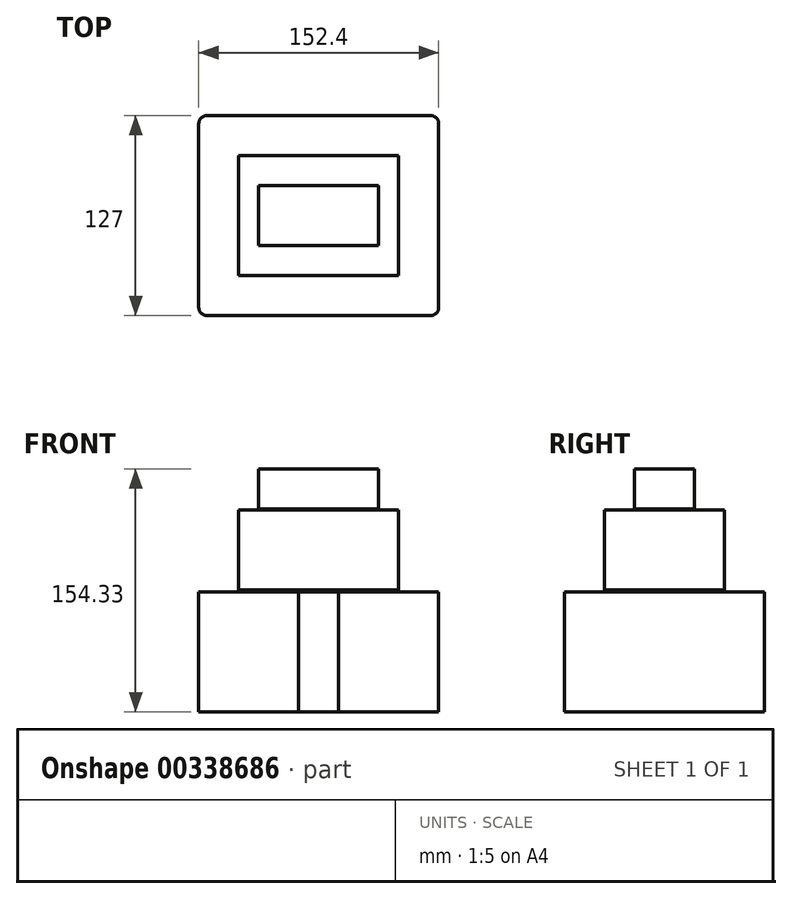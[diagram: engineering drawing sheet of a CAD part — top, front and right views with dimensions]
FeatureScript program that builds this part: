
annotation { "Feature Type Name" : "Feature", "Feature Type Description" : "" }
export const myFeature = defineFeature(function(context is Context, id is Id, definition is map)
    precondition{}
    {
        {
            var Q0;
            Q0=qCreatedBy(makeId("Front.planeOp"),FACE);
            var sketch = newSketch(context, id + "F0", { "sketchPlane" : qUnion([Q0])});
            skLineSegment(sketch, "E0.bottom", {"start": v(-76.2, 38.1) * mm, "end": v(76.2, 38.1) * mm});
            skLineSegment(sketch, "E0.top", {"start": v(-76.2, -38.1) * mm, "end": v(76.2, -38.1) * mm});
            skLineSegment(sketch, "E0.left", {"start": v(-76.2, 38.1) * mm, "end": v(-76.2, -38.1) * mm});
            skLineSegment(sketch, "E0.right", {"start": v(76.2, 38.1) * mm, "end": v(76.2, -38.1) * mm});
            skPoint(sketch, "E0.middle", {"position": v(0, 0) * mm});
            skSolve(sketch);
        }
        {
            var Q0;
            Q0=makeQuery(id+"F0.imprint","IMPRINT",FACE,{"disambiguationData":[TD([[makeQuery(id+"F0.imprint","IMPRINT",EDGE,{"derivedFrom":sQuery(id+"F0.wireOp",EDGE,"E0.bottom")}),-1.0]])]});
            extrude(context, id + "F1", {"entities" : qUnion([Q0]), "endBound" : BoundingType.SYMMETRIC, "depth" : 127 * mm});
        }
        {
            var Q0;
            Q0=qCreatedBy(makeId("Front.planeOp"),FACE);
            var sketch = newSketch(context, id + "F2", { "sketchPlane" : qUnion([Q0])});
            skLineSegment(sketch, "E1.bottom", {"start": v(-50.8, 39.3) * mm, "end": v(50.8, 39.3) * mm});
            skLineSegment(sketch, "E1.top", {"start": v(-50.8, 90.1) * mm, "end": v(50.8, 90.1) * mm});
            skLineSegment(sketch, "E1.left", {"start": v(-50.8, 39.3) * mm, "end": v(-50.8, 90.1) * mm});
            skLineSegment(sketch, "E1.right", {"start": v(50.8, 39.3) * mm, "end": v(50.8, 90.1) * mm});
            skPoint(sketch, "E1.middle", {"position": v(0, 64.7) * mm});
            skSolve(sketch);
        }
        {
            var Q0;
            Q0=makeQuery(id+"F2.imprint","IMPRINT",FACE,{"disambiguationData":[TD([[makeQuery(id+"F2.imprint","IMPRINT",EDGE,{"derivedFrom":sQuery(id+"F2.wireOp",EDGE,"E1.bottom")}),1.0]])]});
            extrude(context, id + "F3", {"entities" : qUnion([Q0]), "endBound" : BoundingType.SYMMETRIC, "depth" : 76.2 * mm});
        }
        {
            var Q0;
            Q0=qCreatedBy(makeId("Front.planeOp"),FACE);
            var sketch = newSketch(context, id + "F4", { "sketchPlane" : qUnion([Q0])});
            skLineSegment(sketch, "E2.bottom", {"start": v(-38.1, 116.23) * mm, "end": v(38.1, 116.23) * mm});
            skLineSegment(sketch, "E2.top", {"start": v(-38.1, 90.83) * mm, "end": v(38.1, 90.83) * mm});
            skLineSegment(sketch, "E2.left", {"start": v(-38.1, 116.23) * mm, "end": v(-38.1, 90.83) * mm});
            skLineSegment(sketch, "E2.right", {"start": v(38.1, 116.23) * mm, "end": v(38.1, 90.83) * mm});
            skPoint(sketch, "E2.middle", {"position": v(0, 103.53) * mm});
            skSolve(sketch);
        }
        {
            var Q0;
            Q0 = qSketchRegion(id + "F4", true);
            extrude(context, id + "F5", {"entities" : qUnion([Q0]), "endBound" : BoundingType.SYMMETRIC, "depth" : 38.1 * mm});
        }
        {
            var Q0;
            Q0=makeQuery(id+"F1.opExtrude","CAP_EDGE",EDGE,{"disambiguationData":[OSD([sQuery(id+"F0.wireOp",EDGE,"E0.left")])],"isStart":false});
            var Q1;
            Q1=makeQuery(id+"F1.opExtrude","CAP_EDGE",EDGE,{"disambiguationData":[OSD([sQuery(id+"F0.wireOp",EDGE,"E0.right")])],"isStart":false});
            var Q2;
            Q2=makeQuery(id+"F1.opExtrude","CAP_EDGE",EDGE,{"disambiguationData":[OSD([sQuery(id+"F0.wireOp",EDGE,"E0.right")])],"isStart":true});
            var Q3;
            Q3=makeQuery(id+"F1.opExtrude","CAP_EDGE",EDGE,{"disambiguationData":[OSD([sQuery(id+"F0.wireOp",EDGE,"E0.left")])],"isStart":true});
            fillet(context, id + "F6", {"entities" : qUnion([Q0, Q1, Q2, Q3]), "radius" : 5.08 * mm, "tangentPropagation" : true, "allowEdgeOverflow" : false});
        }
        {
            var Q0;
            Q0=makeQuery(id+"F1.opExtrude","CAP_FACE",FACE,{"disambiguationData":[OSD([sQuery(id+"F0.wireOp",EDGE,"E0.bottom"),sQuery(id+"F0.wireOp",EDGE,"E0.top"),sQuery(id+"F0.wireOp",EDGE,"E0.left"),sQuery(id+"F0.wireOp",EDGE,"E0.right")])],"isStart":false});
            var sketch = newSketch(context, id + "F7", { "sketchPlane" : qUnion([Q0])});
            skLineSegment(sketch, "E3.bottom", {"start": v(-12.7, 38.1) * mm, "end": v(12.7, 38.1) * mm});
            skLineSegment(sketch, "E3.top", {"start": v(-12.7, -38.1) * mm, "end": v(12.7, -38.1) * mm});
            skLineSegment(sketch, "E3.left", {"start": v(-12.7, 38.1) * mm, "end": v(-12.7, -38.1) * mm});
            skLineSegment(sketch, "E3.right", {"start": v(12.7, 38.1) * mm, "end": v(12.7, -38.1) * mm});
            skPoint(sketch, "E3.middle", {"position": v(0, 0) * mm});
            skSolve(sketch);
        }
        {
            var Q0;
            Q0=makeQuery(id+"F7.imprint","IMPRINT",FACE,{"disambiguationData":[TD([[makeQuery(id+"F7.imprint","IMPRINT",EDGE,{"derivedFrom":sQuery(id+"F7.wireOp",EDGE,"E3.bottom")}),-1.0]])]});
            extrude(context, id + "F8", {"entities" : qUnion([Q0]), "operationType" : NewBodyOperationType.ADD, "endBound" : BoundingType.SYMMETRIC, "depth" : 0 * mm});
        }
    });
